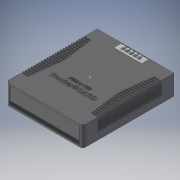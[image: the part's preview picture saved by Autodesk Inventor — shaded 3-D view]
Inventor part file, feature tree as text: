
AUTODESK INVENTOR PART (.ipt)
format: ipt  version: 2016 (Build 200138000, 138)  size: 3,034,112 bytes
history: native  units: mm
features: sketch x30, extrude x25, fillet x4, emboss x4, chamfer x2
ambient origin geometry x8: Origin, YZ Plane, XZ Plane, XY Plane, X Axis, Y Axis, Z Axis, Center Point
bodies: Solid1 (feature_tree)
feature tree (65):
  extrude  "Extrusion1"  Depth=137.0mm
  fillet  "Fillet1"  Radius=30.0mm
  extrude  "Extrusion2"  Depth=15.0mm
  chamfer  "Chamfer1"  Distance=3.0mm
  chamfer  "Chamfer2"  Distance=2.0mm
  extrude  "Extrusion3"  Depth=2.0mm
  extrude  "Extrusion4"  Depth=2.0mm
  extrude  "Extrusion5"  Depth=2.0mm
  sketch  "Sketch6"  dims[d8=15.0mm]
  sketch  "Sketch7"  dims[d9=18.0mm]
  extrude  "Extrusion6"  Depth=2.0mm
  extrude  "Extrusion7"  Depth=3.0mm
  extrude  "Extrusion8"  Depth=2.0mm
  extrude  "Extrusion9"  Depth=3.0mm
  extrude  "Extrusion10"  Depth=2.0mm
  extrude  "Extrusion11"  Depth=3.0mm
  extrude  "Extrusion12"  Depth=2.0mm
  extrude  "Extrusion13"  Depth=3.0mm
  extrude  "Extrusion14"  Depth=2.0mm
  extrude  "Extrusion15"  Depth=3.0mm
  extrude  "Extrusion16"  Depth=2.0mm
  extrude  "Extrusion17"  Depth=3.0mm
  extrude  "Extrusion18"  Depth=2.0mm
  extrude  "Extrusion19"  Depth=3.0mm
  extrude  "Extrusion20"  Depth=2.0mm
  extrude  "Extrusion21"  Depth=3.0mm
  fillet  "Fillet2"  Radius=2.0mm
  fillet  "Fillet3"  Radius=3.0mm
  extrude  "Extrusion22"  Depth=2.0mm
  fillet  "Fillet4"  Radius=3.0mm
  extrude  "Extrusion23"  Depth=2.0mm
  emboss  "Emboss1"
  emboss  "Emboss2"
  extrude  "Extrusion24"  Depth=3.0mm
  extrude  "Extrusion25"  Depth=2.0mm
  sketch  "Sketch29"  dims[d33=2.0mm]
  emboss  "Emboss3"
  emboss  "Emboss4"
  sketch  "Sketch1"  dims[d0=115.0mm d1=137.0mm d2=30.0mm d3=0.0mm]
  sketch  "Sketch2"  dims[d4=5.0mm d5=15.0mm]
  sketch  "Sketch4"  dims[d6=13.0mm]
  sketch  "Sketch5"  dims[d7=20.0mm]
  sketch  "Sketch8"  dims[d10=18.0mm d11=3.0mm d12=0.0mm]
  sketch  "Sketch9"  dims[d13=2.0mm]
  sketch  "Sketch10"  dims[d14=15.0mm]
  sketch  "Sketch11"  dims[d15=10.0mm]
  sketch  "Sketch12"  dims[d16=3.0mm]
  sketch  "Sketch13"  dims[d17=5.0mm]
  sketch  "Sketch14"  dims[d18=5.0mm]
  sketch  "Sketch15"  dims[d19=5.0mm]
  sketch  "Sketch16"  dims[d20=5.0mm]
  sketch  "Sketch17"  dims[d21=5.0mm]
  sketch  "Sketch18"  dims[d22=5.0mm]
  sketch  "Sketch19"  dims[d23=5.0mm]
  sketch  "Sketch20"  dims[d24=5.0mm]
  sketch  "Sketch21"  dims[d25=5.0mm]
  sketch  "Sketch22"  dims[d26=5.0mm]
  sketch  "Sketch23"  dims[d27=5.0mm]
  sketch  "Sketch24"  dims[d28=2.0mm]
  sketch  "Sketch25"  dims[d29=2.0mm]
  sketch  "Sketch26"  dims[d30=2.0mm]
  sketch  "Sketch27"  dims[d31=2.0mm]
  sketch  "Sketch28"  dims[d32=2.0mm]
  sketch  "Sketch30"  dims[d34=2.0mm]
  sketch  "Sketch31"  dims[d35=2.0mm d36=2.0mm d37=2.0mm d38=2.0mm d39=2.0mm d42=2.0mm d43=3.0mm d44=2.0mm d45=3.0mm d46=2.0mm d47=3.0mm d48=2.0mm d49=3.0mm d50=2.0mm d51=3.0mm d52=2.0mm d53=3.0mm d54=2.0mm d55=3.0mm d56=2.0mm d57=3.0mm d58=2.0mm d59=3.0mm d60=2.0mm d61=3.0mm d62=2.0mm d63=3.0mm d64=2.0mm d65=3.0mm d66=2.0mm d67=3.0mm d68=2.0mm d69=3.0mm d70=2.0mm d71=3.0mm d72=2.0mm d73=3.0mm d74=2.0mm d75=3.0mm d76=2.0mm d77=2.0mm d78=15.0mm d120=44.0mm d125=2.0mm d126=3.0mm d127=2.0mm d128=3.0mm d129=2.0mm d130=3.0mm d131=2.0mm d132=3.0mm d133=2.0mm d134=3.0mm d135=2.0mm d136=3.0mm d137=2.0mm d138=3.0mm d139=2.0mm d140=3.0mm d141=2.0mm d142=3.0mm d143=2.0mm d144=3.0mm d145=2.0mm d146=3.0mm d147=2.0mm d148=3.0mm d149=2.0mm d150=3.0mm d151=2.0mm d152=3.0mm d153=2.0mm d154=3.0mm d155=2.0mm d156=3.0mm d157=2.0mm d158=3.0mm d159=2.0mm d160=3.0mm d161=2.0mm d162=15.0mm d163=61.0mm d165=2.0mm d166=3.0mm d167=2.0mm d168=3.0mm d169=2.0mm d170=3.0mm d171=2.0mm d172=3.0mm d173=2.0mm d174=3.0mm d175=2.0mm d176=3.0mm d177=2.0mm d178=3.0mm d179=2.0mm d180=3.0mm d181=2.0mm d182=3.0mm d183=2.0mm d184=45.0deg d185=3.0mm d186=2.0mm d187=45.0deg d188=3.0mm d189=0.0mm d190=17.0mm d191=4.0mm d192=13.0mm d193=60.0mm d194=4.0mm d195=17.0mm d196=1.0mm d197=1.0mm d198=1.0mm d199=1.0mm d200=1.0mm d201=1.0mm d202=1.0mm d203=1.0mm d204=3.0mm d205=0.0mm d206=38.0mm d207=41.0mm d208=38.5mm d209=10.0mm d210=0.5mm d211=0.0mm d212=1.0mm d213=19.0mm d214=20.0mm d215=2.0mm d216=2.0mm d217=2.0mm d218=2.0mm d219=2.0mm d220=2.0mm d221=2.0mm d222=2.0mm d223=2.0mm d224=2.0mm d225=2.0mm d226=2.0mm d227=2.0mm d228=2.0mm d229=2.0mm d230=2.0mm d231=2.0mm d232=2.0mm d233=2.0mm d234=2.0mm d235=2.0mm d236=2.0mm d237=2.0mm d238=2.0mm d239=2.0mm d240=2.0mm d241=2.0mm d242=2.0mm d243=2.0mm d244=2.0mm d245=2.0mm d246=2.0mm d247=2.0mm d248=2.0mm d249=2.0mm d250=2.0mm d251=2.0mm d252=2.0mm d253=2.0mm d254=2.0mm d255=2.0mm d256=2.0mm d257=2.0mm d258=2.0mm d259=2.0mm d260=2.0mm d261=2.0mm d262=3.0mm d263=0.0mm d264=3.0mm d265=0.0mm d267=7.0mm d269=2.0mm d270=2.0mm d271=7.5mm d272=2.0mm d273=2.0mm d274=2.0mm d275=2.0mm d276=2.0mm d277=2.0mm d278=2.0mm d279=2.0mm d280=2.0mm d281=2.0mm d282=2.0mm d283=2.0mm d284=2.0mm d285=2.0mm d286=2.0mm d287=2.0mm d288=2.0mm d289=2.0mm d290=2.0mm d291=2.0mm d292=2.0mm d293=2.0mm d294=2.0mm d295=2.0mm d296=2.0mm d297=2.0mm d298=2.0mm d299=2.0mm d300=2.0mm d301=2.0mm d302=2.0mm d303=2.0mm d304=2.0mm d305=2.0mm d306=2.0mm d307=2.0mm d308=2.0mm d309=2.0mm d310=2.0mm d311=2.0mm d312=2.0mm d313=2.0mm d314=2.0mm d315=2.0mm d316=7.5mm d317=8.0mm d318=8.0mm d319=8.5mm d320=8.5mm d321=9.0mm d322=9.0mm d323=9.5mm d324=9.5mm d325=10.0mm d326=10.0mm d327=10.5mm d328=10.5mm d329=11.0mm d330=11.0mm d331=11.5mm d332=11.5mm d333=12.0mm d334=12.0mm d335=12.5mm d336=12.5mm d337=12.5mm d338=12.5mm d339=12.5mm d340=7.5mm d341=7.5mm d342=8.0mm d343=8.0mm d344=8.5mm d345=8.5mm d346=9.0mm d347=9.0mm d348=9.5mm d349=9.5mm d350=10.0mm d351=10.0mm d352=10.5mm d353=10.5mm d354=11.0mm d355=11.0mm d356=11.5mm d357=11.5mm d358=12.0mm d359=12.0mm d360=12.5mm d361=3.0mm d362=0.0mm d363=7.0mm d364=2.0mm d365=2.0mm d366=2.0mm d367=2.0mm d368=2.0mm d369=2.0mm d370=2.0mm d371=2.0mm d372=2.0mm d373=2.0mm d374=2.0mm d375=2.0mm d376=2.0mm d377=2.0mm d378=2.0mm d379=2.0mm d380=2.0mm d381=2.0mm d382=2.0mm d383=2.0mm d384=2.0mm d385=2.0mm d386=2.0mm d387=2.0mm d388=2.0mm d389=2.0mm d390=2.0mm d391=2.0mm d392=2.0mm d393=2.0mm d394=2.0mm d395=2.0mm d396=2.0mm d397=2.0mm d398=2.0mm d399=2.0mm d400=2.0mm d401=2.0mm d402=2.0mm d403=2.0mm d404=2.0mm d405=2.0mm d406=2.0mm d407=2.0mm d408=2.0mm d409=2.0mm d410=2.0mm d411=0.5mm d412=0.5mm d413=1.0mm d414=1.0mm d415=1.5mm d416=1.5mm d417=2.0mm d418=2.0mm d419=2.5mm d420=2.5mm d421=3.0mm d422=3.0mm d423=3.5mm d424=3.5mm d425=4.0mm d426=4.0mm d427=4.5mm d428=4.5mm d429=5.0mm d430=5.0mm d431=5.5mm d432=0.5mm d433=1.0mm d434=1.5mm d435=2.0mm d436=2.5mm d437=3.0mm d438=3.5mm d439=4.0mm d440=4.5mm d441=5.0mm d442=5.5mm d443=3.0mm d444=0.0mm d445=8.0mm d446=8.5mm d447=3.0mm d448=0.0mm d449=104.0mm d450=25.0mm d451=0.5mm d452=0.0mm d453=5.0mm d454=0.3mm d455=0.0mm d456=2.5mm d457=10.0mm d458=2.5mm d459=8.0mm d460=2.0mm d461=0.0mm d462=20.0mm d463=1.0mm d464=0.3mm d465=0.0mm d466=70.0mm d467=12.0mm d468=8.0mm d469=8.0mm d470=0.5mm d471=0.0mm d472=13.0mm d478=0.5mm d484=1.0mm d486=13.0mm d487=13.0mm d488=13.0mm d489=13.0mm d490=1.0mm d491=1.0mm d492=1.0mm d493=1.0mm d494=8.0mm d495=2.0mm d496=8.0mm d497=2.0mm d498=8.0mm d499=2.0mm d500=8.0mm d501=2.0mm d502=8.0mm d503=2.0mm d504=5.0mm d505=2.0mm d506=5.0mm d507=2.0mm d508=5.0mm d509=2.0mm d510=5.0mm d511=2.0mm d512=5.0mm d513=2.0mm d514=22.0mm d515=0.0mm d516=113.0mm d517=27.0mm d518=1.0mm d519=0.2mm d520=0.0mm d521=32.0mm d522=19.0mm d523=0.0mm d524=0.2mm d525=0.0mm d526=8.0mm d527=3.0mm d528=0.1mm d529=0.0mm d530=7.0mm d531=2.5mm d532=15.0mm d533=0.0mm d534=2.5mm d535=15.0mm d536=0.0mm d537=2.5mm d538=1.25mm d539=15.0mm d540=0.0mm d541=1.0mm d542=3.5mm d543=3.5mm d544=3.5mm d545=3.5mm d546=0.1mm d547=0.0mm d548=0.1mm d549=0.0mm d550=0.1mm d551=0.0mm d552=42.0mm d553=11.0mm d554=1.0mm d555=0.1mm d556=0.0mm d557=28.0mm d558=4.0mm d559=4.0mm d560=2.0mm d561=4.0mm d562=2.0mm d563=4.0mm d564=2.0mm d565=4.0mm d566=2.0mm d567=0.1mm d568=0.0mm d569=0.1mm d570=0.0mm d571=0.5mm d572=0.0mm]
